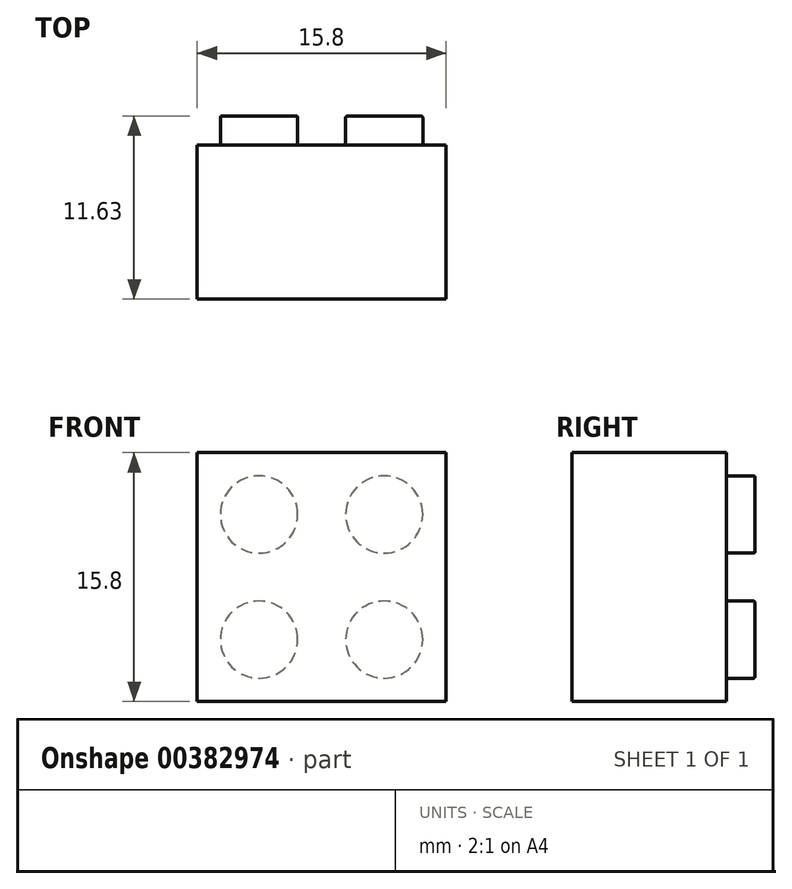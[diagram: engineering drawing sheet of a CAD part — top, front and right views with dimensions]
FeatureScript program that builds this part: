
annotation { "Feature Type Name" : "Feature", "Feature Type Description" : "" }
export const myFeature = defineFeature(function(context is Context, id is Id, definition is map)
    precondition{}
    {
        {
            var Q0;
            Q0=qCreatedBy(makeId("Front.planeOp"),FACE);
            var sketch = newSketch(context, id + "F0", { "sketchPlane" : qUnion([Q0])});
            skLineSegment(sketch, "E0", {"start": v(2.76, 15.8) * mm, "end": v(2.76, 0) * mm});
            skLineSegment(sketch, "E1", {"start": v(2.76, 0) * mm, "end": v(18.56, 0) * mm});
            skLineSegment(sketch, "E2", {"start": v(18.56, 0) * mm, "end": v(18.56, 15.8) * mm});
            skLineSegment(sketch, "E3", {"start": v(18.56, 15.8) * mm, "end": v(2.76, 15.8) * mm});
            skSolve(sketch);
        }
        {
            var Q0;
            Q0=makeQuery(id+"F0.imprint","IMPRINT",FACE,{"disambiguationData":[TD([[makeQuery(id+"F0.imprint","IMPRINT",EDGE,{"derivedFrom":sQuery(id+"F0.wireOp",EDGE,"E0")}),1.0]])]});
            extrude(context, id + "F1", {"entities" : qUnion([Q0]), "depth" : 9.8 * mm});
        }
        {
            var Q0;
            Q0=qCreatedBy(makeId("Front.planeOp"),FACE);
            var sketch = newSketch(context, id + "F2", { "sketchPlane" : qUnion([Q0])});
            skCircle(sketch, "E4", {"center": v(6.69, 11.88) * mm, "radius": 2.45 * mm});
            skCircle(sketch, "E5", {"center": v(14.64, 11.88) * mm, "radius": 2.45 * mm});
            skCircle(sketch, "E6", {"center": v(6.69, 3.93) * mm, "radius": 2.45 * mm});
            skCircle(sketch, "E7", {"center": v(14.64, 3.93) * mm, "radius": 2.45 * mm});
            skSolve(sketch);
        }
        {
            var Q0;
            Q0=qSketchRegion(id+"F2",true);
            extrude(context, id + "F3", {"entities" : qUnion([Q0]), "operationType" : NewBodyOperationType.ADD, "oppositeDirection" : true, "depth" : 1.83 * mm});
        }
        {
            var Q0;
            Q0=makeQuery(id+"F3.opExtrude","CAP_FACE",FACE,{"disambiguationData":[OSD([sQuery(id+"F2.wireOp",EDGE,"E5")])],"isStart":false});
            var Q1;
            Q1=makeQuery(id+"F3.opExtrude","CAP_FACE",FACE,{"disambiguationData":[OSD([sQuery(id+"F2.wireOp",EDGE,"E4")])],"isStart":false});
            var Q2;
            Q2=makeQuery(id+"F3.opExtrude","CAP_FACE",FACE,{"disambiguationData":[OSD([sQuery(id+"F2.wireOp",EDGE,"E6")])],"isStart":false});
            var Q3;
            Q3=makeQuery(id+"F3.opExtrude","CAP_FACE",FACE,{"disambiguationData":[OSD([sQuery(id+"F2.wireOp",EDGE,"E7")])],"isStart":false});
            fillet(context, id + "F4", {"entities" : qUnion([Q0, Q1, Q2, Q3]), "radius" : 0.1 * mm, "tangentPropagation" : true, "allowEdgeOverflow" : false});
        }
    });
